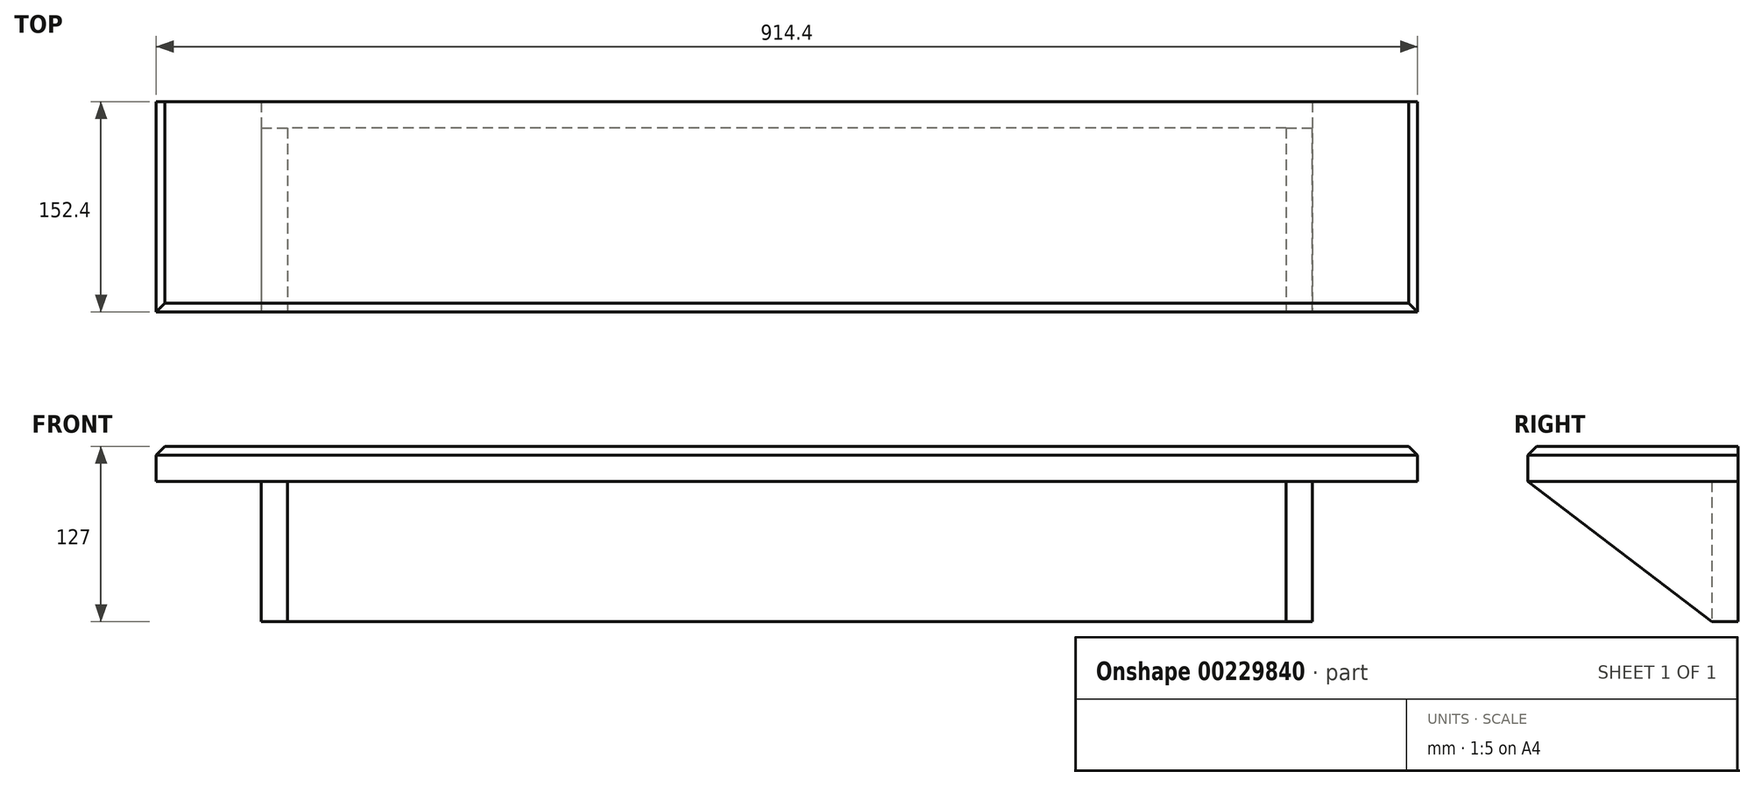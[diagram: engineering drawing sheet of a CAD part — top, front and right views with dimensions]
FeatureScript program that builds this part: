
annotation { "Feature Type Name" : "Feature", "Feature Type Description" : "" }
export const myFeature = defineFeature(function(context is Context, id is Id, definition is map)
    precondition{}
    {
        {
            var Q0;
            Q0=qCreatedBy(makeId("Front.planeOp"),FACE);
            var sketch = newSketch(context, id + "F0", { "sketchPlane" : qUnion([Q0])});
            skLineSegment(sketch, "E0.bottom", {"start": v(-457.2, 12.7) * mm, "end": v(457.2, 12.7) * mm});
            skLineSegment(sketch, "E0.top", {"start": v(-457.2, -12.7) * mm, "end": v(457.2, -12.7) * mm});
            skLineSegment(sketch, "E0.left", {"start": v(-457.2, 12.7) * mm, "end": v(-457.2, -12.7) * mm});
            skLineSegment(sketch, "E0.right", {"start": v(457.2, 12.7) * mm, "end": v(457.2, -12.7) * mm});
            skSolve(sketch);
        }
        {
            var Q0;
            Q0 = qSketchRegion(id + "F0", true);
            extrude(context, id + "F1", {"entities" : qUnion([Q0]), "depth" : 152.4 * mm});
        }
        {
            var Q0;
            Q0=makeQuery(id+"F1.opExtrude","SWEPT_EDGE",EDGE,{"disambiguationData":[OSD([sQuery(id+"F0.wireOp",EDGE,"E0.bottom"),sQuery(id+"F0.wireOp",EDGE,"E0.left")])]});
            var Q1;
            Q1=makeQuery(id+"F1.opExtrude","CAP_EDGE",EDGE,{"disambiguationData":[OSD([sQuery(id+"F0.wireOp",EDGE,"E0.bottom")])],"isStart":false});
            var Q2;
            Q2=makeQuery(id+"F1.opExtrude","SWEPT_EDGE",EDGE,{"disambiguationData":[OSD([sQuery(id+"F0.wireOp",EDGE,"E0.bottom"),sQuery(id+"F0.wireOp",EDGE,"E0.right")])]});
            chamfer(context, id + "F2", {"entities" : qUnion([Q0, Q1, Q2]), "width" : 6.35 * mm, "tangentPropagation" : true});
        }
        {
            var Q0;
            Q0=makeQuery(id+"F1.opExtrude","SWEPT_FACE",FACE,{"disambiguationData":[OSD([sQuery(id+"F0.wireOp",EDGE,"E0.top")])]});
            var sketch = newSketch(context, id + "F3", { "sketchPlane" : qUnion([Q0])});
            skLineSegment(sketch, "E1.bottom", {"start": v(-381, 0) * mm, "end": v(-361.95, 0) * mm});
            skLineSegment(sketch, "E1.top", {"start": v(-381, 152.4) * mm, "end": v(-361.95, 152.4) * mm});
            skLineSegment(sketch, "E1.left", {"start": v(-381, 0) * mm, "end": v(-381, 152.4) * mm});
            skLineSegment(sketch, "E1.right", {"start": v(-361.95, 0) * mm, "end": v(-361.95, 152.4) * mm});
            skLineSegment(sketch, "E2.MirrorCS", {"start": v(361.95, 0) * mm, "end": v(361.95, 152.4) * mm});
            skLineSegment(sketch, "E3.MirrorCS", {"start": v(381, 0) * mm, "end": v(361.95, 0) * mm});
            skLineSegment(sketch, "E4.MirrorCS", {"start": v(381, 152.4) * mm, "end": v(361.95, 152.4) * mm});
            skLineSegment(sketch, "E5.MirrorCS", {"start": v(381, 0) * mm, "end": v(381, 152.4) * mm});
            skSolve(sketch);
        }
        {
            var Q0;
            Q0 = qSketchRegion(id + "F3", true);
            extrude(context, id + "F4", {"entities" : qUnion([Q0]), "operationType" : NewBodyOperationType.ADD, "depth" : 101.6 * mm});
        }
        {
            var Q0;
            Q0=makeQuery(id+"F4.opExtrude","SWEPT_FACE",FACE,{"disambiguationData":[OSD([sQuery(id+"F3.wireOp",EDGE,"E5.MirrorCS")])]});
            var sketch = newSketch(context, id + "F5", { "sketchPlane" : qUnion([Q0])});
            skLineSegment(sketch, "E6", {"start": v(-152.4, -12.7) * mm, "end": v(-19.05, -114.3) * mm});
            skLineSegment(sketch, "E7", {"start": v(-19.05, -114.3) * mm, "end": v(-152.4, -114.3) * mm});
            skLineSegment(sketch, "E8", {"start": v(-152.4, -114.3) * mm, "end": v(-152.4, -12.7) * mm});
            skSolve(sketch);
        }
        {
            var Q0;
            Q0 = qSketchRegion(id + "F5", true);
            extrude(context, id + "F6", {"entities" : qUnion([Q0]), "operationType" : NewBodyOperationType.REMOVE, "endBound" : BoundingType.THROUGH_ALL, "oppositeDirection" : true, "depth" : 25.4 * mm});
        }
        {
            var Q0;
            Q0=makeQuery(id+"F4.opExtrude","SWEPT_FACE",FACE,{"disambiguationData":[OSD([sQuery(id+"F3.wireOp",EDGE,"E1.right")])]});
            var sketch = newSketch(context, id + "F7", { "sketchPlane" : qUnion([Q0])});
            skLineSegment(sketch, "E9", {"start": v(0, -114.3) * mm, "end": v(-19.05, -114.3) * mm});
            skLineSegment(sketch, "E10", {"start": v(-19.05, -114.3) * mm, "end": v(-19.05, -12.7) * mm});
            skLineSegment(sketch, "E11", {"start": v(-19.05, -12.7) * mm, "end": v(0, -12.7) * mm});
            skLineSegment(sketch, "E12", {"start": v(0, -12.7) * mm, "end": v(0, -114.3) * mm});
            skSolve(sketch);
        }
        {
            var Q0;
            Q0 = qSketchRegion(id + "F7", true);
            var Q1;
            Q1=makeQuery(id+"F4.opExtrude","SWEPT_FACE",FACE,{"disambiguationData":[OSD([sQuery(id+"F3.wireOp",EDGE,"E2.MirrorCS")])]});
            extrude(context, id + "F8", {"entities" : qUnion([Q0]), "operationType" : NewBodyOperationType.ADD, "endBound" : BoundingType.UP_TO_SURFACE, "endBoundEntityFace" : qUnion([Q1]), "depth" : 25.4 * mm});
        }
    });
